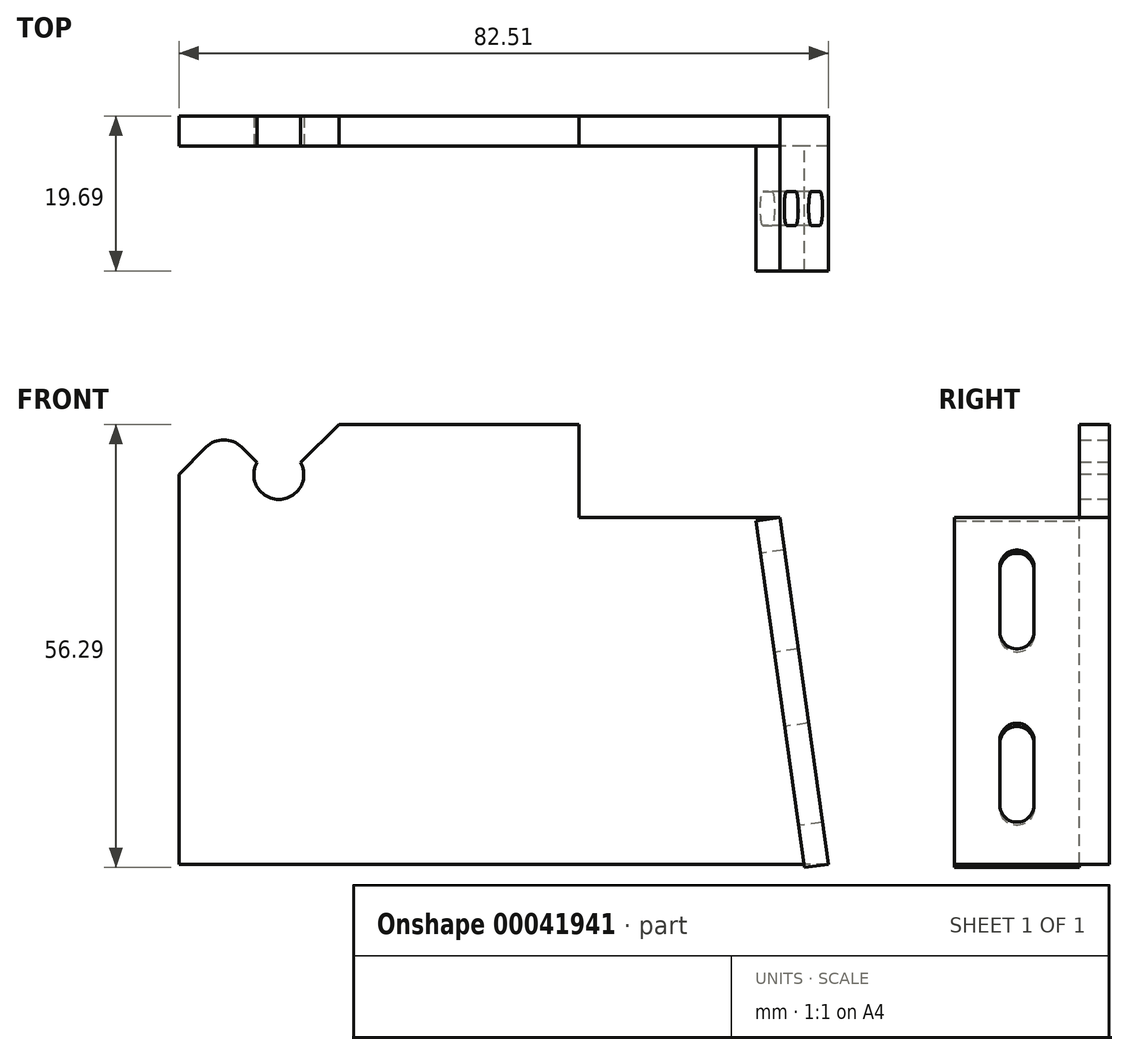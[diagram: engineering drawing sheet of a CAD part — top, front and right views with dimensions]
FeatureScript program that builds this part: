
annotation { "Feature Type Name" : "Feature", "Feature Type Description" : "" }
export const myFeature = defineFeature(function(context is Context, id is Id, definition is map)
    precondition{}
    {
        {
            var Q0;
            Q0=qCreatedBy(makeId("Front.planeOp"),FACE);
            var sketch = newSketch(context, id + "F0", { "sketchPlane" : qUnion([Q0])});
            skLineSegment(sketch, "E0", {"start": v(3.02, -43.6) * mm, "end": v(9.2, -87.62) * mm});
            skLineSegment(sketch, "E1", {"start": v(9.2, -87.62) * mm, "end": v(6.19, -88.04) * mm});
            skLineSegment(sketch, "E2", {"start": v(6.19, -88.04) * mm, "end": v(0, -44.02) * mm});
            skLineSegment(sketch, "E3", {"start": v(0, -44.02) * mm, "end": v(3.02, -43.6) * mm});
            skLineSegment(sketch, "E4", {"start": v(0, 0) * mm, "end": v(43.58, 0) * mm, "construction": true});
            skPoint(sketch, "E5", {"position": v(4.48, -53.98) * mm});
            skPoint(sketch, "E6", {"position": v(7.57, -75.98) * mm});
            skSolve(sketch);
        }
        {
            var Q0;
            Q0=qSketchRegion(id+"F0",true);
            extrude(context, id + "F1", {"entities" : qUnion([Q0]), "depth" : 15.88 * mm});
        }
        {
            var Q0;
            Q0=makeQuery(id+"F1.opExtrude","SWEPT_FACE",FACE,{"disambiguationData":[OSD([sQuery(id+"F0.wireOp",EDGE,"E2")])]});
            var sketch = newSketch(context, id + "F2", { "sketchPlane" : qUnion([Q0])});
            skLineSegment(sketch, "E7.bottom", {"start": v(5.78, -47.72) * mm, "end": v(10.1, -47.72) * mm});
            skLineSegment(sketch, "E7.top", {"start": v(5.78, -60.42) * mm, "end": v(10.1, -60.42) * mm});
            skLineSegment(sketch, "E7.left", {"start": v(5.78, -47.72) * mm, "end": v(5.78, -60.42) * mm});
            skLineSegment(sketch, "E7.right", {"start": v(10.1, -47.72) * mm, "end": v(10.1, -60.42) * mm});
            skLineSegment(sketch, "E8.bottom", {"start": v(5.78, -69.95) * mm, "end": v(10.1, -69.95) * mm});
            skLineSegment(sketch, "E8.top", {"start": v(5.78, -82.65) * mm, "end": v(10.1, -82.65) * mm});
            skLineSegment(sketch, "E8.left", {"start": v(5.78, -69.95) * mm, "end": v(5.78, -82.65) * mm});
            skLineSegment(sketch, "E8.right", {"start": v(10.1, -69.95) * mm, "end": v(10.1, -82.65) * mm});
            skPoint(sketch, "E9", {"position": v(10.1, -54.07) * mm});
            skLineSegment(sketch, "E10", {"start": v(7.94, -43.6) * mm, "end": v(7.94, -47.72) * mm, "construction": true});
            skSolve(sketch);
        }
        {
            var Q0;
            Q0=qSketchRegion(id+"F2",true);
            extrude(context, id + "F3", {"entities" : qUnion([Q0]), "operationType" : NewBodyOperationType.REMOVE, "endBound" : BoundingType.THROUGH_ALL, "oppositeDirection" : true, "depth" : 25.4 * mm});
        }
        {
            var Q0;
            Q0=makeQuery(id+"F3.boolean.opBoolean","COPY",EDGE,{"derivedFrom":makeQuery(id+"F3.opExtrude","SWEPT_EDGE",EDGE,{"disambiguationData":[OSD([sQuery(id+"F2.wireOp",EDGE,"E7.bottom"),sQuery(id+"F2.wireOp",EDGE,"E7.left")])]})});
            var Q1;
            Q1=makeQuery(id+"F3.boolean.opBoolean","COPY",EDGE,{"derivedFrom":makeQuery(id+"F3.opExtrude","SWEPT_EDGE",EDGE,{"disambiguationData":[OSD([sQuery(id+"F2.wireOp",EDGE,"E8.bottom"),sQuery(id+"F2.wireOp",EDGE,"E8.left")])]})});
            var Q2;
            Q2=makeQuery(id+"F3.boolean.opBoolean","COPY",EDGE,{"derivedFrom":makeQuery(id+"F3.opExtrude","SWEPT_EDGE",EDGE,{"disambiguationData":[OSD([sQuery(id+"F2.wireOp",EDGE,"E8.bottom"),sQuery(id+"F2.wireOp",EDGE,"E8.right")])]})});
            var Q3;
            Q3=makeQuery(id+"F3.boolean.opBoolean","COPY",EDGE,{"derivedFrom":makeQuery(id+"F3.opExtrude","SWEPT_EDGE",EDGE,{"disambiguationData":[OSD([sQuery(id+"F2.wireOp",EDGE,"E7.bottom"),sQuery(id+"F2.wireOp",EDGE,"E7.right")])]})});
            var Q4;
            Q4=makeQuery(id+"F3.boolean.opBoolean","COPY",EDGE,{"derivedFrom":makeQuery(id+"F3.opExtrude","SWEPT_EDGE",EDGE,{"disambiguationData":[OSD([sQuery(id+"F2.wireOp",EDGE,"E7.top"),sQuery(id+"F2.wireOp",EDGE,"E7.right")])]})});
            var Q5;
            Q5=makeQuery(id+"F3.boolean.opBoolean","COPY",EDGE,{"derivedFrom":makeQuery(id+"F3.opExtrude","SWEPT_EDGE",EDGE,{"disambiguationData":[OSD([sQuery(id+"F2.wireOp",EDGE,"E8.top"),sQuery(id+"F2.wireOp",EDGE,"E8.right")])]})});
            var Q6;
            Q6=makeQuery(id+"F3.boolean.opBoolean","COPY",EDGE,{"derivedFrom":makeQuery(id+"F3.opExtrude","SWEPT_EDGE",EDGE,{"disambiguationData":[OSD([sQuery(id+"F2.wireOp",EDGE,"E8.top"),sQuery(id+"F2.wireOp",EDGE,"E8.left")])]})});
            var Q7;
            Q7=makeQuery(id+"F3.boolean.opBoolean","COPY",EDGE,{"derivedFrom":makeQuery(id+"F3.opExtrude","SWEPT_EDGE",EDGE,{"disambiguationData":[OSD([sQuery(id+"F2.wireOp",EDGE,"E7.top"),sQuery(id+"F2.wireOp",EDGE,"E7.left")])]})});
            fillet(context, id + "F4", {"entities" : qUnion([Q0, Q1, Q2, Q3, Q4, Q5, Q6, Q7]), "radius" : 2.16 * mm, "tangentPropagation" : true, "allowEdgeOverflow" : false});
        }
        {
            var Q0;
            Q0=qCreatedBy(makeId("Front.planeOp"),FACE);
            var sketch = newSketch(context, id + "F5", { "sketchPlane" : qUnion([Q0])});
            skLineSegment(sketch, "E11", {"start": v(3.02, -43.6) * mm, "end": v(9.2, -87.62) * mm});
            skLineSegment(sketch, "E12", {"start": v(9.2, -87.62) * mm, "end": v(-73.31, -87.62) * mm});
            skLineSegment(sketch, "E13", {"start": v(-73.31, -87.62) * mm, "end": v(-73.31, -25.4) * mm});
            skLineSegment(sketch, "E14", {"start": v(-73.31, -25.4) * mm, "end": v(-22.51, -25.4) * mm});
            skLineSegment(sketch, "E15", {"start": v(-22.51, -25.4) * mm, "end": v(-22.51, -43.6) * mm});
            skLineSegment(sketch, "E16", {"start": v(-22.51, -43.6) * mm, "end": v(3.02, -43.6) * mm});
            skCircle(sketch, "E17", {"center": v(-60.61, -38.1) * mm, "radius": 3.18 * mm});
            skSolve(sketch);
        }
        {
            var Q0;
            Q0=qSketchRegion(id+"F5",true);
            extrude(context, id + "F6", {"entities" : qUnion([Q0]), "operationType" : NewBodyOperationType.ADD, "oppositeDirection" : true, "depth" : 3.8 * mm});
        }
        {
            var Q0;
            Q0=qCreatedBy(makeId("Front.planeOp"),FACE);
            var sketch = newSketch(context, id + "F7", { "sketchPlane" : qUnion([Q0])});
            skLineSegment(sketch, "E18", {"start": v(-60.61, -25.4) * mm, "end": v(-73.31, -38.1) * mm});
            skLineSegment(sketch, "E19", {"start": v(-73.31, -38.1) * mm, "end": v(-73.31, -25.4) * mm});
            skLineSegment(sketch, "E20", {"start": v(-73.31, -25.4) * mm, "end": v(-60.61, -25.4) * mm});
            skSolve(sketch);
        }
        {
            var Q0;
            Q0 = qSketchRegion(id + "F7", true);
            extrude(context, id + "F8", {"entities" : qUnion([Q0]), "operationType" : NewBodyOperationType.REMOVE, "oppositeDirection" : true, "depth" : 25.4 * mm});
        }
        {
            var Q0;
            Q0=qCreatedBy(makeId("Front.planeOp"),FACE);
            var sketch = newSketch(context, id + "F9", { "sketchPlane" : qUnion([Q0])});
            skLineSegment(sketch, "E21", {"start": v(-60.61, -39.39) * mm, "end": v(-74.6, -25.4) * mm});
            skLineSegment(sketch, "E22", {"start": v(-74.6, -25.4) * mm, "end": v(-22.51, -25.4) * mm});
            skLineSegment(sketch, "E23", {"start": v(-22.51, -25.4) * mm, "end": v(-22.51, -31.75) * mm});
            skLineSegment(sketch, "E24", {"start": v(-22.51, -31.75) * mm, "end": v(-52.98, -31.75) * mm});
            skLineSegment(sketch, "E25", {"start": v(-52.98, -31.75) * mm, "end": v(-60.61, -39.39) * mm});
            skLineSegment(sketch, "E26", {"start": v(-63.4, -36.6) * mm, "end": v(-57.82, -36.6) * mm, "construction": true});
            skSolve(sketch);
        }
        {
            var Q0;
            Q0 = qSketchRegion(id + "F9", true);
            extrude(context, id + "F10", {"entities" : qUnion([Q0]), "operationType" : NewBodyOperationType.REMOVE, "oppositeDirection" : true, "depth" : 25.4 * mm});
        }
        {
            var Q0;
            Q0=makeQuery(id+"F10.boolean.opBoolean","INTERSECT",EDGE,{"derivedFrom":[makeQuery(id+"F8.boolean.opBoolean","COPY",FACE,{"derivedFrom":makeQuery(id+"F8.opExtrude","SWEPT_FACE",FACE,{"disambiguationData":[OSD([sQuery(id+"F7.wireOp",EDGE,"E18")])]})}),makeQuery(id+"F10.opExtrude","SWEPT_FACE",FACE,{"disambiguationData":[OSD([sQuery(id+"F9.wireOp",EDGE,"E21")])]})]});
            fillet(context, id + "F11", {"entities" : qUnion([Q0]), "radius" : 3.17 * mm, "tangentPropagation" : true, "allowEdgeOverflow" : false});
        }
    });
